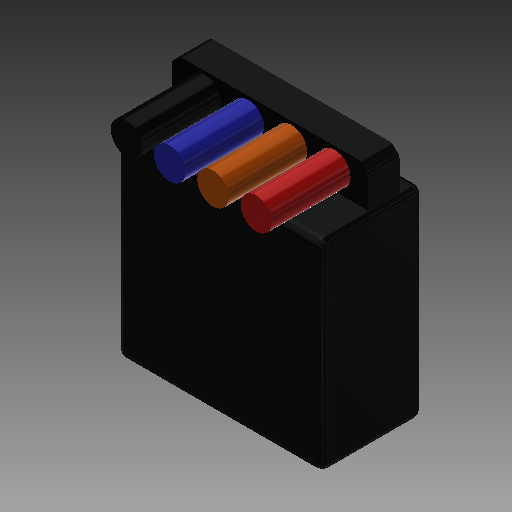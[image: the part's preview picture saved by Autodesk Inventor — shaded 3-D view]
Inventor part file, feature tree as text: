
AUTODESK INVENTOR PART (.ipt)
format: ipt  version: 2020 (Build 240168000, 168)  size: 215,040 bytes
history: native  units: mm
features: other x6, sketch x4, extrude x3, fillet x2, chamfer x1, projected_geometry x1
ambient origin geometry x1: Origin
bodies: Body1 (feature_tree)
feature tree (17):
  other  "ソリッド1"
  extrude  "外形"  Depth=25.7mm
  other  "作業平面1"
  extrude  "突起部"  Depth=26.2mm
  chamfer  "面取り1"  Distance=12.9mm
  fillet  "フィレット1"  Radius=5.0mm
  fillet  "フィレット2"  Radius=25.0mm
  sketch  "スケッチ3"
  other  "作業点1"
  other  "作業点2"
  other  "作業点3"
  other  "作業点4"
  extrude  "押し出し3"  Depth=4.0mm TaperAngle=0.0deg
  sketch  "スケッチ1"
  sketch  "スケッチ2"
  projected_geometry  "投影ループ1"
  sketch  "スケッチ4"
